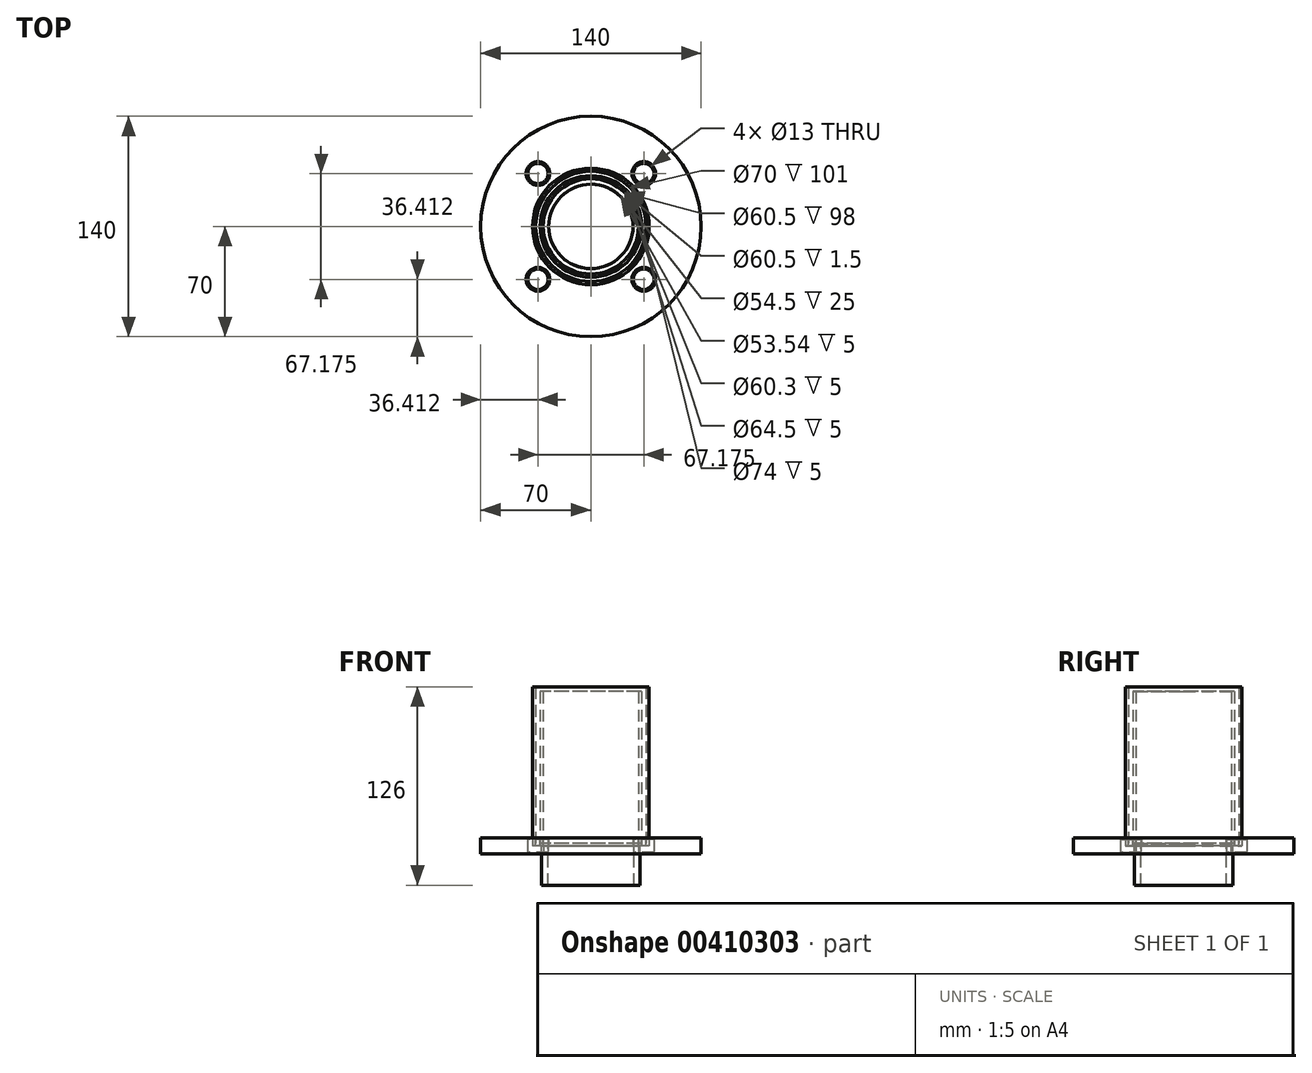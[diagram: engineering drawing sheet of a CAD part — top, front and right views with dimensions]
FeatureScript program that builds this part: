
annotation { "Feature Type Name" : "Feature", "Feature Type Description" : "" }
export const myFeature = defineFeature(function(context is Context, id is Id, definition is map)
    precondition{}
    {
        {
            var Q0;
            Q0=qCreatedBy(makeId("Top.planeOp"),FACE);
            var sketch = newSketch(context, id + "F0", { "sketchPlane" : qUnion([Q0])});
            skCircle(sketch, "E0", {"center": v(0, 0) * mm, "radius": 70 * mm});
            skCircle(sketch, "E1", {"center": v(-33.59, 33.59) * mm, "radius": 6.5 * mm});
            skCircle(sketch, "E2.1.0", {"center": v(-33.59, -33.59) * mm, "radius": 6.5 * mm});
            skCircle(sketch, "E2.2.0", {"center": v(33.59, -33.59) * mm, "radius": 6.5 * mm});
            skCircle(sketch, "E2.3.0", {"center": v(33.59, 33.59) * mm, "radius": 6.5 * mm});
            skCircle(sketch, "E3", {"center": v(0, 0) * mm, "radius": 26.77 * mm});
            skLineSegment(sketch, "E4", {"start": v(0, 0) * mm, "end": v(-49.5, 49.5) * mm, "construction": true});
            skSolve(sketch);
        }
        {
            var Q0;
            Q0=makeQuery(id+"F0.imprint","IMPRINT",FACE,{"disambiguationData":[TD([[makeQuery(id+"F0.imprint","IMPRINT",EDGE,{"derivedFrom":sQuery(id+"F0.wireOp",EDGE,"E0")}),1.0]])]});
            extrude(context, id + "F1", {"entities" : qUnion([Q0]), "depth" : 10 * mm});
        }
        {
            var Q0;
            Q0=makeQuery(id+"F1.opExtrude","CAP_FACE",FACE,{"disambiguationData":[OSD([sQuery(id+"F0.wireOp",EDGE,"E0"),sQuery(id+"F0.wireOp",EDGE,"E1"),sQuery(id+"F0.wireOp",EDGE,"E2.1.0"),sQuery(id+"F0.wireOp",EDGE,"E2.2.0"),sQuery(id+"F0.wireOp",EDGE,"E2.3.0"),sQuery(id+"F0.wireOp",EDGE,"E3")])],"isStart":true});
            var sketch = newSketch(context, id + "F2", { "sketchPlane" : qUnion([Q0])});
            skCircle(sketch, "E5", {"center": v(0, 0) * mm, "radius": 30.15 * mm});
            skSolve(sketch);
        }
        {
            var Q0;
            Q0 = qSketchRegion(id + "F2", true);
            extrude(context, id + "F3", {"entities" : qUnion([Q0]), "operationType" : NewBodyOperationType.REMOVE, "oppositeDirection" : true, "depth" : 5 * mm});
        }
        {
            var Q0;
            Q0=makeQuery(id+"F3.boolean.opBoolean","COPY",FACE,{"derivedFrom":makeQuery(id+"F3.opExtrude","CAP_FACE",FACE,{"disambiguationData":[OSD([sQuery(id+"F2.wireOp",EDGE,"E5")])],"isStart":false})});
            var sketch = newSketch(context, id + "F4", { "sketchPlane" : qUnion([Q0])});
            skCircle(sketch, "E6", {"center": v(0, 0) * mm, "radius": 31.25 * mm});
            skCircle(sketch, "E7", {"center": v(0, 0) * mm, "radius": 27.25 * mm});
            skSolve(sketch);
        }
        {
            var Q0;
            Q0 = qSketchRegion(id + "F4", true);
            extrude(context, id + "F5", {"entities" : qUnion([Q0]), "depth" : 25 * mm});
        }
        {
            var Q0;
            Q0=makeQuery(id+"F1.opExtrude","CAP_EDGE",EDGE,{"disambiguationData":[OSD([sQuery(id+"F0.wireOp",EDGE,"E1")])],"isStart":true});
            var Q1;
            Q1=makeQuery(id+"F1.opExtrude","CAP_EDGE",EDGE,{"disambiguationData":[OSD([sQuery(id+"F0.wireOp",EDGE,"E2.3.0")])],"isStart":true});
            var Q2;
            Q2=makeQuery(id+"F1.opExtrude","CAP_EDGE",EDGE,{"disambiguationData":[OSD([sQuery(id+"F0.wireOp",EDGE,"E2.2.0")])],"isStart":true});
            var Q3;
            Q3=makeQuery(id+"F1.opExtrude","CAP_EDGE",EDGE,{"disambiguationData":[OSD([sQuery(id+"F0.wireOp",EDGE,"E2.1.0")])],"isStart":true});
            var Q4;
            Q4=makeQuery(id+"F1.opExtrude","CAP_EDGE",EDGE,{"disambiguationData":[OSD([sQuery(id+"F0.wireOp",EDGE,"E2.3.0")])],"isStart":false});
            var Q5;
            Q5=makeQuery(id+"F1.opExtrude","CAP_EDGE",EDGE,{"disambiguationData":[OSD([sQuery(id+"F0.wireOp",EDGE,"E2.2.0")])],"isStart":false});
            var Q6;
            Q6=makeQuery(id+"F1.opExtrude","CAP_EDGE",EDGE,{"disambiguationData":[OSD([sQuery(id+"F0.wireOp",EDGE,"E2.1.0")])],"isStart":false});
            var Q7;
            Q7=makeQuery(id+"F1.opExtrude","CAP_EDGE",EDGE,{"disambiguationData":[OSD([sQuery(id+"F0.wireOp",EDGE,"E1")])],"isStart":false});
            chamfer(context, id + "F6", {"entities" : qUnion([Q0, Q1, Q2, Q3, Q4, Q5, Q6, Q7]), "width" : 1 * mm, "tangentPropagation" : true});
        }
        {
            var Q0;
            Q0=makeQuery(id+"F1.opExtrude","CAP_FACE",FACE,{"disambiguationData":[OSD([sQuery(id+"F0.wireOp",EDGE,"E0"),sQuery(id+"F0.wireOp",EDGE,"E1"),sQuery(id+"F0.wireOp",EDGE,"E2.1.0"),sQuery(id+"F0.wireOp",EDGE,"E2.2.0"),sQuery(id+"F0.wireOp",EDGE,"E2.3.0"),sQuery(id+"F0.wireOp",EDGE,"E3")])],"isStart":false});
            var sketch = newSketch(context, id + "F7", { "sketchPlane" : qUnion([Q0])});
            skCircle(sketch, "E8", {"center": v(0, 0) * mm, "radius": 30.25 * mm});
            skCircle(sketch, "E9", {"center": v(0, 0) * mm, "radius": 32.25 * mm});
            skSolve(sketch);
        }
        {
            var Q0;
            Q0 = qSketchRegion(id + "F7", true);
            extrude(context, id + "F8", {"entities" : qUnion([Q0]), "operationType" : NewBodyOperationType.REMOVE, "oppositeDirection" : true, "depth" : 5 * mm});
        }
        {
            var Q0;
            {var subQ0=sQuery(id+"F0.wireOp",EDGE,"E2.2.0");var subQ1=sQuery(id+"F0.wireOp",EDGE,"E2.1.0");var subQ2=sQuery(id+"F0.wireOp",EDGE,"E1");var subQ3=sQuery(id+"F0.wireOp",EDGE,"E0");var subQ4=sQuery(id+"F0.wireOp",EDGE,"E2.3.0");Q0=makeQuery(id+"F8.boolean.opBoolean","SPLIT",FACE,{"disambiguationData":[TD([makeQuery(id+"F1.opExtrude","SWEPT_FACE",FACE,{"disambiguationData":[OSD([subQ3])]})])],"derivedFrom":makeQuery(id+"F1.opExtrude","CAP_FACE",FACE,{"disambiguationData":[OSD([subQ3,subQ2,subQ1,subQ0,subQ4,sQuery(id+"F0.wireOp",EDGE,"E3")])],"isStart":false})});}
            var sketch = newSketch(context, id + "F9", { "sketchPlane" : qUnion([Q0])});
            skCircle(sketch, "E10", {"center": v(0, 0) * mm, "radius": 35 * mm});
            skCircle(sketch, "E11", {"center": v(0, 0) * mm, "radius": 37 * mm});
            skSolve(sketch);
        }
        {
            var Q0;
            Q0 = qSketchRegion(id + "F9", true);
            extrude(context, id + "F10", {"entities" : qUnion([Q0]), "operationType" : NewBodyOperationType.REMOVE, "oppositeDirection" : true, "depth" : 5 * mm});
        }
        {
            var Q0;
            Q0=makeQuery(id+"F8.boolean.opBoolean","COPY",FACE,{"derivedFrom":makeQuery(id+"F8.opExtrude","CAP_FACE",FACE,{"disambiguationData":[OSD([sQuery(id+"F7.wireOp",EDGE,"E8"),sQuery(id+"F7.wireOp",EDGE,"E9")])],"isStart":false})});
            var sketch = newSketch(context, id + "F11", { "sketchPlane" : qUnion([Q0])});
            skCircle(sketch, "E12", {"center": v(0, 0) * mm, "radius": 32.25 * mm});
            skCircle(sketch, "E13", {"center": v(0, 0) * mm, "radius": 30.25 * mm});
            skSolve(sketch);
        }
        {
            var Q0;
            Q0 = qSketchRegion(id + "F11", true);
            extrude(context, id + "F12", {"entities" : qUnion([Q0]), "depth" : 98 * mm});
        }
        {
            var Q0;
            Q0=makeQuery(id+"F10.boolean.opBoolean","COPY",FACE,{"derivedFrom":makeQuery(id+"F10.opExtrude","CAP_FACE",FACE,{"disambiguationData":[OSD([sQuery(id+"F9.wireOp",EDGE,"E10"),sQuery(id+"F9.wireOp",EDGE,"E11")])],"isStart":false})});
            var sketch = newSketch(context, id + "F13", { "sketchPlane" : qUnion([Q0])});
            skCircle(sketch, "E14", {"center": v(0, 0) * mm, "radius": 35 * mm});
            skCircle(sketch, "E15", {"center": v(0, 0) * mm, "radius": 37 * mm});
            skSolve(sketch);
        }
        {
            var Q0;
            Q0 = qSketchRegion(id + "F13", true);
            extrude(context, id + "F14", {"entities" : qUnion([Q0]), "depth" : 101 * mm});
        }
        {
            var Q0;
            Q0=makeQuery(id+"F8.boolean.opBoolean","COPY",FACE,{"derivedFrom":makeQuery(id+"F8.opExtrude","CAP_FACE",FACE,{"disambiguationData":[OSD([sQuery(id+"F7.wireOp",EDGE,"E8"),sQuery(id+"F7.wireOp",EDGE,"E9")])],"isStart":false})});
            var sketch = newSketch(context, id + "F15", { "sketchPlane" : qUnion([Q0])});
            skCircle(sketch, "E16", {"center": v(0, 0) * mm, "radius": 30.25 * mm});
            skCircle(sketch, "E17", {"center": v(0, 0) * mm, "radius": 32.25 * mm});
            skSolve(sketch);
        }
        {
            var Q0;
            Q0 = qSketchRegion(id + "F15", true);
            extrude(context, id + "F16", {"entities" : qUnion([Q0]), "depth" : 1.5 * mm});
        }
    });
